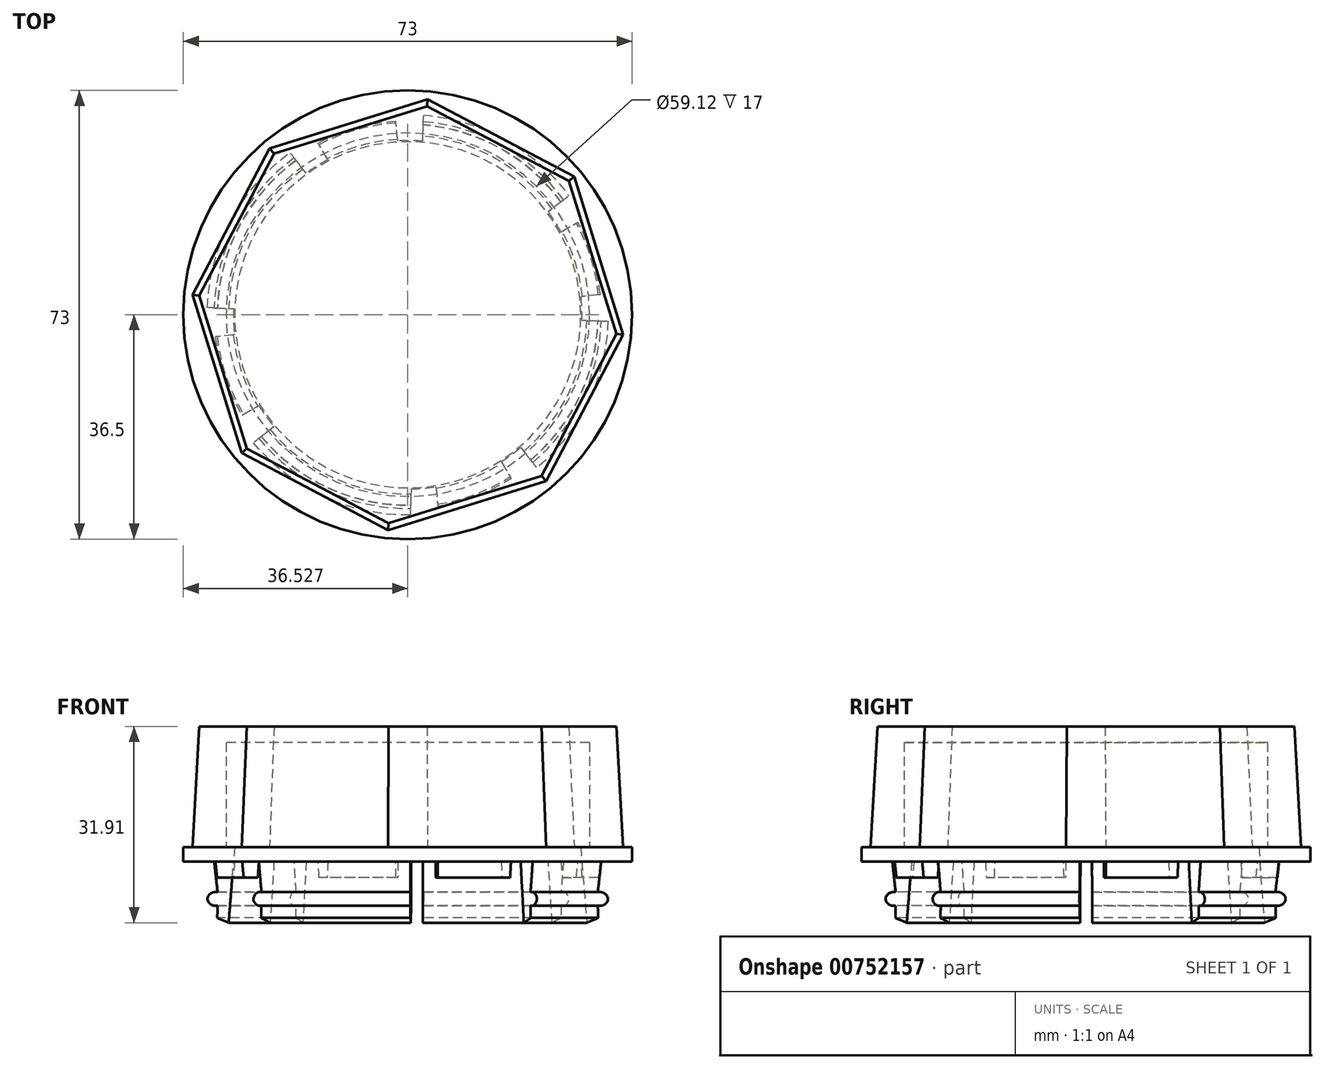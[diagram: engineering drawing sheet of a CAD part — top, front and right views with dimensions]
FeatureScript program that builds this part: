
annotation { "Feature Type Name" : "Feature", "Feature Type Description" : "" }
export const myFeature = defineFeature(function(context is Context, id is Id, definition is map)
    precondition{}
    {
        {
            var Q0;
            Q0=qCreatedBy(makeId("Top.planeOp"),FACE);
            var sketch = newSketch(context, id + "F0", { "sketchPlane" : qUnion([Q0])});
            skCircle(sketch, "E0.cCircle", {"center": v(41.88, 0) * mm, "radius": 35.18 * mm, "construction": true});
            skLineSegment(sketch, "E0.0", {"start": v(14.82, -22.49) * mm, "end": v(6.85, 3.23) * mm});
            skLineSegment(sketch, "E0.1", {"start": v(6.85, 3.23) * mm, "end": v(19.39, 27.05) * mm});
            skLineSegment(sketch, "E0.2", {"start": v(19.39, 27.05) * mm, "end": v(45.1, 35.03) * mm});
            skLineSegment(sketch, "E0.3", {"start": v(45.1, 35.03) * mm, "end": v(68.93, 22.49) * mm});
            skLineSegment(sketch, "E0.4", {"start": v(68.93, 22.49) * mm, "end": v(76.9, -3.23) * mm});
            skLineSegment(sketch, "E0.5", {"start": v(76.9, -3.23) * mm, "end": v(64.36, -27.05) * mm});
            skLineSegment(sketch, "E0.6", {"start": v(64.36, -27.05) * mm, "end": v(38.65, -35.03) * mm});
            skLineSegment(sketch, "E0.7", {"start": v(38.65, -35.03) * mm, "end": v(14.82, -22.49) * mm});
            skSolve(sketch);
        }
        {
            var Q0;
            Q0=qSketchRegion(id+"F0",true);
            extrude(context, id + "F1", {"entities" : qUnion([Q0]), "depth" : 19.6 * mm, "offsetDistance" : 25 * mm, "hasDraft" : true, "draftAngle" : 3 * degree, "draftPullDirection" : true});
        }
        {
            var Q0;
            Q0=qCreatedBy(makeId("Front.planeOp"),FACE);
            var sketch = newSketch(context, id + "F2", { "sketchPlane" : qUnion([Q0])});
            skLineSegment(sketch, "E1", {"start": v(71.3, 19.61) * mm, "end": v(71.3, 20.31) * mm});
            skLineSegment(sketch, "E2", {"start": v(71.3, 20.31) * mm, "end": v(70.7, 20.31) * mm});
            skLineSegment(sketch, "E3", {"start": v(70.7, 20.31) * mm, "end": v(70.7, 19.61) * mm});
            skLineSegment(sketch, "E4", {"start": v(61.4, 22) * mm, "end": v(61.4, 21.36) * mm});
            skLineSegment(sketch, "E5", {"start": v(61.4, 21.36) * mm, "end": v(41.94, 21.36) * mm});
            skArc(sketch, "E6", {"start": v(70.7, 19.61) * mm, "mid": v(66.19, 21.38) * mm, "end": v(61.4, 22) * mm});
            skLineSegment(sketch, "E7", {"start": v(41.94, 21.36) * mm, "end": v(41.94, 19.6) * mm});
            skSolve(sketch);
        }
        {
            var Q0;
            Q0=qSketchRegion(id+"F2",true);
            var Q1;
            Q1=sQuery(id+"F2.wireOp",EDGE,"E5");
            var Q2;
            Q2=sQuery(id+"F2.wireOp",EDGE,"E4");
            var Q3;
            Q3=sQuery(id+"F2.wireOp",EDGE,"E6");
            var Q4;
            Q4=sQuery(id+"F2.wireOp",EDGE,"E1");
            var Q5;
            Q5=sQuery(id+"F2.wireOp",EDGE,"E3");
            var Q6;
            Q6=sQuery(id+"F2.wireOp",EDGE,"E2");
            var Q7;
            Q7=sQuery(id+"F2.wireOp",EDGE,"E7");
            revolve(context, id + "F3", {"bodyType" : ToolBodyType.SURFACE, "surfaceOperationType" : NewSurfaceOperationType.NEW, "entities" : qUnion([Q0]), "surfaceEntities" : qUnion([Q1, Q2, Q3, Q4, Q5, Q6]), "axis" : qUnion([Q7]), "revolveType" : RevolveType.FULL});
        }
        {
            var Q0;
            Q0=qCreatedBy(makeId("Front.planeOp"),FACE);
            var sketch = newSketch(context, id + "F4", { "sketchPlane" : qUnion([Q0])});
            skLineSegment(sketch, "E8", {"start": v(41.85, 2.47) * mm, "end": v(41.85, -0.28) * mm});
            skLineSegment(sketch, "E9", {"start": v(13.92, 0) * mm, "end": v(10.66, 0) * mm});
            skLineSegment(sketch, "E10", {"start": v(13.7, 0) * mm, "end": v(12.7, -12.3) * mm});
            skLineSegment(sketch, "E11", {"start": v(12.7, -12.3) * mm, "end": v(10.85, -11.54) * mm});
            skLineSegment(sketch, "E12", {"start": v(10.85, -11.54) * mm, "end": v(10.9, -9.54) * mm});
            skLineSegment(sketch, "E13", {"start": v(10.9, -7.32) * mm, "end": v(10.35, -2.35) * mm});
            skLineSegment(sketch, "E14", {"start": v(41.85, 0) * mm, "end": v(5.35, 0) * mm});
            skLineSegment(sketch, "E15", {"start": v(41.85, 2.47) * mm, "end": v(41.85, -22.81) * mm});
            skPoint(sketch, "E16", {"position": v(5.35, -2.35) * mm});
            skLineSegment(sketch, "E17", {"start": v(5.35, -2.35) * mm, "end": v(10.35, -2.35) * mm});
            skLineSegment(sketch, "E18", {"start": v(5.35, 0) * mm, "end": v(5.35, -2.35) * mm});
            skPoint(sketch, "E19", {"position": v(10.85, 0) * mm});
            skFitSpline(sketch, "E20", {"points": [v(10.9, -7.32) * mm, v(9.26, -8.52) * mm, v(10.9, -9.54) * mm], "startDerivative": vector(-5.91, 0.78) * mm, "endDerivative": vector(4.99, 1.1) * mm});
            skSolve(sketch);
        }
        {
            var Q0;
            Q0=qSketchRegion(id+"F4",true);
            var Q1;
            Q1=sQuery(id+"F4.wireOp",EDGE,"E14");
            var Q2;
            Q2=sQuery(id+"F4.wireOp",EDGE,"4cd7ZZWE-5ar5-vtm7-FDXw-HXyrbe5Stu3w");
            var Q3;
            Q3=sQuery(id+"F4.wireOp",EDGE,"E13");
            var Q4;
            Q4=sQuery(id+"F4.wireOp",EDGE,"4DvQKk0b-5Hhs-ZDoF-mvT5-3W0hP7iMOcEj");
            var Q5;
            Q5=sQuery(id+"F4.wireOp",EDGE,"seUdqvdR-pzSz-YYxp-RZCM-9PM7dyDkCj1m");
            var Q6;
            Q6=sQuery(id+"F4.wireOp",EDGE,"E11");
            var Q7;
            Q7=sQuery(id+"F4.wireOp",EDGE,"E12");
            var Q8;
            Q8=sQuery(id+"F4.wireOp",EDGE,"E10");
            var Q9;
            Q9=sQuery(id+"F4.wireOp",EDGE,"E15");
            revolve(context, id + "F5", {"surfaceOperationType" : NewSurfaceOperationType.NEW, "entities" : qUnion([Q0]), "surfaceEntities" : qUnion([Q1, Q2, Q3, Q4, Q5, Q6, Q7, Q8]), "axis" : qUnion([Q9]), "revolveType" : RevolveType.FULL});
        }
        {
            var Q0;
            Q0=qCreatedBy(makeId("Top.planeOp"),FACE);
            var sketch = newSketch(context, id + "F6", { "sketchPlane" : qUnion([Q0])});
            skCircle(sketch, "E21", {"center": v(41.88, 0) * mm, "radius": 29.56 * mm});
            skSolve(sketch);
        }
        {
            var Q0;
            Q0=qSketchRegion(id+"F6",true);
            extrude(context, id + "F7", {"entities" : qUnion([Q0]), "operationType" : NewBodyOperationType.REMOVE, "depth" : 17 * mm, "offsetDistance" : 25 * mm});
        }
        {
            var Q0;
            Q0=qCreatedBy(makeId("Top.planeOp"),FACE);
            var sketch = newSketch(context, id + "F8", { "sketchPlane" : qUnion([Q0])});
            skText(sketch, "E22", { "text": "SAAB", "fontName": "OpenSans-Bold.ttf"});
            const initialGuessF8  = {"E22": [0.03239, -0.00298, 1, 0, 0.00593]};
            skSetInitialGuess(sketch, initialGuessF8);
            skSolve(sketch);
        }
        {
            var Q0;
            Q0=qCreatedBy(makeId("Top.planeOp"),FACE);
            var sketch = newSketch(context, id + "F9", { "sketchPlane" : qUnion([Q0])});
            skLineSegment(sketch, "E23", {"start": v(69.85, -34.13) * mm, "end": v(16.32, 34.78) * mm});
            skLineSegment(sketch, "E24", {"start": v(16.32, 34.78) * mm, "end": v(43.91, 43.26) * mm});
            skLineSegment(sketch, "E25", {"start": v(43.91, 43.26) * mm, "end": v(42.61, -43.16) * mm});
            skLineSegment(sketch, "E26", {"start": v(9.14, -26.59) * mm, "end": v(79.03, 27.7) * mm});
            skLineSegment(sketch, "E27", {"start": v(79.03, 27.7) * mm, "end": v(86.57, -0.61) * mm});
            skLineSegment(sketch, "E28", {"start": v(86.57, -0.61) * mm, "end": v(43.22, 0) * mm});
            skLineSegment(sketch, "E29", {"start": v(42.61, -43.16) * mm, "end": v(69.85, -34.13) * mm});
            skLineSegment(sketch, "E30", {"start": v(0, 0.68) * mm, "end": v(43.22, 0) * mm});
            skLineSegment(sketch, "E31", {"start": v(9.14, -26.59) * mm, "end": v(0, 0.68) * mm});
            skPoint(sketch, "E32", {"position": v(19.48, -18.55) * mm});
            skPoint(sketch, "E33", {"position": v(12.6, 0.48) * mm});
            skPoint(sketch, "E34", {"position": v(24.83, 23.83) * mm});
            skPoint(sketch, "E35", {"position": v(42.83, -28.88) * mm});
            skPoint(sketch, "E36", {"position": v(60.43, -22) * mm});
            skPoint(sketch, "E37", {"position": v(71.17, -0.4) * mm});
            skPoint(sketch, "E38", {"position": v(65.22, 16.98) * mm});
            skPoint(sketch, "E39", {"position": v(43.69, 28.4) * mm});
            skLineSegment(sketch, "E40", {"start": v(12.6, 0.48) * mm, "end": v(19.48, -18.55) * mm});
            skLineSegment(sketch, "E41", {"start": v(24.83, 23.83) * mm, "end": v(43.69, 28.4) * mm});
            skLineSegment(sketch, "E42", {"start": v(65.22, 16.98) * mm, "end": v(71.17, -0.4) * mm});
            skLineSegment(sketch, "E43", {"start": v(60.43, -22) * mm, "end": v(42.83, -28.88) * mm});
            skSolve(sketch);
        }
        {
            var Q0;
            Q0=qSketchRegion(id+"F9",true);
            extrude(context, id + "F10", {"entities" : qUnion([Q0]), "oppositeDirection" : true, "depth" : 25 * mm, "offsetDistance" : 25 * mm, "hasSecondDirection" : true, "secondDirectionOppositeDirection" : true, "secondDirectionDepth" : 5 * mm});
        }
        {
            var Q0;
            Q0=makeQuery(id+"F10.opExtrude","SWEPT_BODY",BODY,{"disambiguationData":[OSD([sQuery(id+"F9.wireOp",EDGE,"E23"),sQuery(id+"F9.wireOp",EDGE,"E25"),sQuery(id+"F9.wireOp",EDGE,"E26"),sQuery(id+"F9.wireOp",EDGE,"E28"),sQuery(id+"F9.wireOp",EDGE,"E29"),sQuery(id+"F9.wireOp",EDGE,"E30"),sQuery(id+"F9.wireOp",EDGE,"E31")])]});
            var Q1;
            Q1=makeQuery(id+"F10.opExtrude","SWEPT_BODY",BODY,{"disambiguationData":[OSD([sQuery(id+"F9.wireOp",EDGE,"E26"),sQuery(id+"F9.wireOp",EDGE,"E27"),sQuery(id+"F9.wireOp",EDGE,"E28")])]});
            var Q2;
            Q2=makeQuery(id+"F10.opExtrude","SWEPT_BODY",BODY,{"disambiguationData":[OSD([sQuery(id+"F9.wireOp",EDGE,"E23"),sQuery(id+"F9.wireOp",EDGE,"E24"),sQuery(id+"F9.wireOp",EDGE,"E25")])]});
            var Q3;
            Q3=makeQuery(id+"FadKjfFnsJpzDV8_9.opBoolean","SPLIT",BODY,{"disambiguationData":[OD(5.0)],"derivedFrom":makeQuery(id+"F5.opRevolve","SWEPT_BODY",BODY,{"disambiguationData":[OSD([sQuery(id+"F4.wireOp",EDGE,"E10"),sQuery(id+"F4.wireOp",EDGE,"E11"),sQuery(id+"F4.wireOp",EDGE,"E12"),sQuery(id+"F4.wireOp",EDGE,"seUdqvdR-pzSz-YYxp-RZCM-9PM7dyDkCj1m"),sQuery(id+"F4.wireOp",EDGE,"4DvQKk0b-5Hhs-ZDoF-mvT5-3W0hP7iMOcEj"),sQuery(id+"F4.wireOp",EDGE,"E13"),sQuery(id+"F4.wireOp",EDGE,"E14"),sQuery(id+"F4.wireOp",EDGE,"E17"),sQuery(id+"F4.wireOp",EDGE,"E18")])]})});
            var Q4;
            Q4=makeQuery(id+"FadKjfFnsJpzDV8_9.opBoolean","SPLIT",BODY,{"disambiguationData":[OD(3.0)],"derivedFrom":makeQuery(id+"F5.opRevolve","SWEPT_BODY",BODY,{"disambiguationData":[OSD([sQuery(id+"F4.wireOp",EDGE,"E10"),sQuery(id+"F4.wireOp",EDGE,"E11"),sQuery(id+"F4.wireOp",EDGE,"E12"),sQuery(id+"F4.wireOp",EDGE,"seUdqvdR-pzSz-YYxp-RZCM-9PM7dyDkCj1m"),sQuery(id+"F4.wireOp",EDGE,"4DvQKk0b-5Hhs-ZDoF-mvT5-3W0hP7iMOcEj"),sQuery(id+"F4.wireOp",EDGE,"E13"),sQuery(id+"F4.wireOp",EDGE,"E14"),sQuery(id+"F4.wireOp",EDGE,"E17"),sQuery(id+"F4.wireOp",EDGE,"E18")])]})});
            var Q5;
            Q5=makeQuery(id+"FadKjfFnsJpzDV8_9.opBoolean","SPLIT",BODY,{"disambiguationData":[OD(7.0)],"derivedFrom":makeQuery(id+"F5.opRevolve","SWEPT_BODY",BODY,{"disambiguationData":[OSD([sQuery(id+"F4.wireOp",EDGE,"E10"),sQuery(id+"F4.wireOp",EDGE,"E11"),sQuery(id+"F4.wireOp",EDGE,"E12"),sQuery(id+"F4.wireOp",EDGE,"seUdqvdR-pzSz-YYxp-RZCM-9PM7dyDkCj1m"),sQuery(id+"F4.wireOp",EDGE,"4DvQKk0b-5Hhs-ZDoF-mvT5-3W0hP7iMOcEj"),sQuery(id+"F4.wireOp",EDGE,"E13"),sQuery(id+"F4.wireOp",EDGE,"E14"),sQuery(id+"F4.wireOp",EDGE,"E17"),sQuery(id+"F4.wireOp",EDGE,"E18")])]})});
            var Q6;
            Q6=makeQuery(id+"FadKjfFnsJpzDV8_9.opBoolean","SPLIT",BODY,{"disambiguationData":[OD(2.0)],"derivedFrom":makeQuery(id+"F5.opRevolve","SWEPT_BODY",BODY,{"disambiguationData":[OSD([sQuery(id+"F4.wireOp",EDGE,"E10"),sQuery(id+"F4.wireOp",EDGE,"E11"),sQuery(id+"F4.wireOp",EDGE,"E12"),sQuery(id+"F4.wireOp",EDGE,"seUdqvdR-pzSz-YYxp-RZCM-9PM7dyDkCj1m"),sQuery(id+"F4.wireOp",EDGE,"4DvQKk0b-5Hhs-ZDoF-mvT5-3W0hP7iMOcEj"),sQuery(id+"F4.wireOp",EDGE,"E13"),sQuery(id+"F4.wireOp",EDGE,"E14"),sQuery(id+"F4.wireOp",EDGE,"E17"),sQuery(id+"F4.wireOp",EDGE,"E18")])]})});
            var Q7;
            Q7=makeQuery(id+"FadKjfFnsJpzDV8_9.opBoolean","SPLIT",BODY,{"disambiguationData":[OD(0.0)],"derivedFrom":makeQuery(id+"F5.opRevolve","SWEPT_BODY",BODY,{"disambiguationData":[OSD([sQuery(id+"F4.wireOp",EDGE,"E10"),sQuery(id+"F4.wireOp",EDGE,"E11"),sQuery(id+"F4.wireOp",EDGE,"E12"),sQuery(id+"F4.wireOp",EDGE,"seUdqvdR-pzSz-YYxp-RZCM-9PM7dyDkCj1m"),sQuery(id+"F4.wireOp",EDGE,"4DvQKk0b-5Hhs-ZDoF-mvT5-3W0hP7iMOcEj"),sQuery(id+"F4.wireOp",EDGE,"E13"),sQuery(id+"F4.wireOp",EDGE,"E14"),sQuery(id+"F4.wireOp",EDGE,"E17"),sQuery(id+"F4.wireOp",EDGE,"E18")])]})});
            var Q8;
            Q8=makeQuery(id+"FadKjfFnsJpzDV8_9.opBoolean","SPLIT",BODY,{"disambiguationData":[OD(6.0)],"derivedFrom":makeQuery(id+"F5.opRevolve","SWEPT_BODY",BODY,{"disambiguationData":[OSD([sQuery(id+"F4.wireOp",EDGE,"E10"),sQuery(id+"F4.wireOp",EDGE,"E11"),sQuery(id+"F4.wireOp",EDGE,"E12"),sQuery(id+"F4.wireOp",EDGE,"seUdqvdR-pzSz-YYxp-RZCM-9PM7dyDkCj1m"),sQuery(id+"F4.wireOp",EDGE,"4DvQKk0b-5Hhs-ZDoF-mvT5-3W0hP7iMOcEj"),sQuery(id+"F4.wireOp",EDGE,"E13"),sQuery(id+"F4.wireOp",EDGE,"E14"),sQuery(id+"F4.wireOp",EDGE,"E17"),sQuery(id+"F4.wireOp",EDGE,"E18")])]})});
            var Q9;
            Q9=makeQuery(id+"FadKjfFnsJpzDV8_9.opBoolean","SPLIT",BODY,{"disambiguationData":[OD(4.0)],"derivedFrom":makeQuery(id+"F5.opRevolve","SWEPT_BODY",BODY,{"disambiguationData":[OSD([sQuery(id+"F4.wireOp",EDGE,"E10"),sQuery(id+"F4.wireOp",EDGE,"E11"),sQuery(id+"F4.wireOp",EDGE,"E12"),sQuery(id+"F4.wireOp",EDGE,"seUdqvdR-pzSz-YYxp-RZCM-9PM7dyDkCj1m"),sQuery(id+"F4.wireOp",EDGE,"4DvQKk0b-5Hhs-ZDoF-mvT5-3W0hP7iMOcEj"),sQuery(id+"F4.wireOp",EDGE,"E13"),sQuery(id+"F4.wireOp",EDGE,"E14"),sQuery(id+"F4.wireOp",EDGE,"E17"),sQuery(id+"F4.wireOp",EDGE,"E18")])]})});
            var Q10;
            Q10=makeQuery(id+"FadKjfFnsJpzDV8_9.opBoolean","SPLIT",BODY,{"disambiguationData":[OD(1.0)],"derivedFrom":makeQuery(id+"F5.opRevolve","SWEPT_BODY",BODY,{"disambiguationData":[OSD([sQuery(id+"F4.wireOp",EDGE,"E10"),sQuery(id+"F4.wireOp",EDGE,"E11"),sQuery(id+"F4.wireOp",EDGE,"E12"),sQuery(id+"F4.wireOp",EDGE,"seUdqvdR-pzSz-YYxp-RZCM-9PM7dyDkCj1m"),sQuery(id+"F4.wireOp",EDGE,"4DvQKk0b-5Hhs-ZDoF-mvT5-3W0hP7iMOcEj"),sQuery(id+"F4.wireOp",EDGE,"E13"),sQuery(id+"F4.wireOp",EDGE,"E14"),sQuery(id+"F4.wireOp",EDGE,"E17"),sQuery(id+"F4.wireOp",EDGE,"E18")])]})});
            booleanBodies(context, id + "F11", {"operationType" : BooleanOperationType.SUBTRACTION, "tools" : qUnion([Q0, Q1, Q2]), "targets" : qUnion([Q3, Q4, Q5, Q6, Q7, Q8, Q9, Q10])});
        }
        {
            var Q0;
            Q0=qCreatedBy(makeId("Top.planeOp"),FACE);
            var sketch = newSketch(context, id + "F12", { "sketchPlane" : qUnion([Q0])});
            skPoint(sketch, "E44.endSnap0", {"position": v(222.12, 4.24) * mm});
            skPoint(sketch, "E45", {"position": v(43.35, 0) * mm});
            skLineSegment(sketch, "E46", {"start": v(76.6, 26.03) * mm, "end": v(5.98, -29.26) * mm});
            skLineSegment(sketch, "E47", {"start": v(43.35, 0) * mm, "end": v(74.1, -39.28) * mm});
            skLineSegment(sketch, "E48", {"start": v(43.35, 0) * mm, "end": v(14.72, 36.58) * mm});
            skLineSegment(sketch, "E49", {"start": v(1.61, -23.99) * mm, "end": v(43.35, 0) * mm});
            skLineSegment(sketch, "E50", {"start": v(43.35, 0) * mm, "end": v(69.77, -45.97) * mm});
            skLineSegment(sketch, "E51", {"start": v(43.35, 0) * mm, "end": v(81.27, 21.79) * mm});
            skLineSegment(sketch, "E52", {"start": v(43.35, 0) * mm, "end": v(20.03, 40.59) * mm});
            skLineSegment(sketch, "E53", {"start": v(14.72, 36.58) * mm, "end": v(20.03, 40.59) * mm});
            skLineSegment(sketch, "E54", {"start": v(76.6, 26.03) * mm, "end": v(81.27, 21.79) * mm});
            skLineSegment(sketch, "E55", {"start": v(74.1, -39.28) * mm, "end": v(69.77, -45.97) * mm});
            skLineSegment(sketch, "E56", {"start": v(5.98, -29.26) * mm, "end": v(1.61, -23.99) * mm});
            skLineSegment(sketch, "E57", {"start": v(85.32, 4.6) * mm, "end": v(-3.82, -5.18) * mm});
            skLineSegment(sketch, "E58", {"start": v(43.35, 0) * mm, "end": v(48.8, -49.6) * mm});
            skLineSegment(sketch, "E59", {"start": v(43.35, 0) * mm, "end": v(38.29, 46.18) * mm});
            skLineSegment(sketch, "E60", {"start": v(-4.76, 1.6) * mm, "end": v(43.35, 0) * mm});
            skLineSegment(sketch, "E61", {"start": v(43.35, 0) * mm, "end": v(41.59, -52.99) * mm});
            skLineSegment(sketch, "E62", {"start": v(43.35, 0) * mm, "end": v(87.06, -1.46) * mm});
            skLineSegment(sketch, "E63", {"start": v(43.35, 0) * mm, "end": v(44.92, 46.79) * mm});
            skLineSegment(sketch, "E64", {"start": v(38.29, 46.18) * mm, "end": v(44.92, 46.79) * mm});
            skLineSegment(sketch, "E65", {"start": v(85.32, 4.6) * mm, "end": v(87.06, -1.46) * mm});
            skLineSegment(sketch, "E66", {"start": v(48.8, -49.6) * mm, "end": v(41.59, -52.99) * mm});
            skLineSegment(sketch, "E67", {"start": v(-3.82, -5.18) * mm, "end": v(-4.76, 1.6) * mm});
            skSolve(sketch);
        }
        {
            var Q0;
            Q0=qSketchRegion(id+"F12",true);
            extrude(context, id + "F13", {"entities" : qUnion([Q0]), "oppositeDirection" : true, "depth" : 10 * mm, "offsetDistance" : 25 * mm});
        }
        {
            var Q0;
            Q0=makeQuery(id+"F13.opExtrude","SWEPT_BODY",BODY,{"disambiguationData":[OSD([sQuery(id+"F12.wireOp",EDGE,"E48"),sQuery(id+"F12.wireOp",EDGE,"E52"),sQuery(id+"F12.wireOp",EDGE,"E53")])]});
            var Q1;
            Q1=makeQuery(id+"F13.opExtrude","SWEPT_BODY",BODY,{"disambiguationData":[OSD([sQuery(id+"F12.wireOp",EDGE,"E57"),sQuery(id+"F12.wireOp",EDGE,"E60"),sQuery(id+"F12.wireOp",EDGE,"E67")])]});
            var Q2;
            Q2=makeQuery(id+"F13.opExtrude","SWEPT_BODY",BODY,{"disambiguationData":[OSD([sQuery(id+"F12.wireOp",EDGE,"E46"),sQuery(id+"F12.wireOp",EDGE,"E49"),sQuery(id+"F12.wireOp",EDGE,"E56")])]});
            var Q3;
            Q3=makeQuery(id+"F13.opExtrude","SWEPT_BODY",BODY,{"disambiguationData":[OSD([sQuery(id+"F12.wireOp",EDGE,"E58"),sQuery(id+"F12.wireOp",EDGE,"E61"),sQuery(id+"F12.wireOp",EDGE,"E66")])]});
            var Q4;
            Q4=makeQuery(id+"F13.opExtrude","SWEPT_BODY",BODY,{"disambiguationData":[OSD([sQuery(id+"F12.wireOp",EDGE,"E47"),sQuery(id+"F12.wireOp",EDGE,"E50"),sQuery(id+"F12.wireOp",EDGE,"E55")])]});
            var Q5;
            Q5=makeQuery(id+"F13.opExtrude","SWEPT_BODY",BODY,{"disambiguationData":[OSD([sQuery(id+"F12.wireOp",EDGE,"E57"),sQuery(id+"F12.wireOp",EDGE,"E62"),sQuery(id+"F12.wireOp",EDGE,"E65")])]});
            var Q6;
            Q6=makeQuery(id+"F13.opExtrude","SWEPT_BODY",BODY,{"disambiguationData":[OSD([sQuery(id+"F12.wireOp",EDGE,"E46"),sQuery(id+"F12.wireOp",EDGE,"E51"),sQuery(id+"F12.wireOp",EDGE,"E54")])]});
            var Q7;
            Q7=makeQuery(id+"F13.opExtrude","SWEPT_BODY",BODY,{"disambiguationData":[OSD([sQuery(id+"F12.wireOp",EDGE,"E59"),sQuery(id+"F12.wireOp",EDGE,"E63"),sQuery(id+"F12.wireOp",EDGE,"E64")])]});
            transform(context, id + "F14", {"entities" : qUnion([Q0, Q1, Q2, Q3, Q4, Q5, Q6, Q7]), "transformType" : TransformType.TRANSLATION_3D, "dx" : 0 * mm, "dy" : 0 * mm, "dz" : -2.35 * mm, "makeCopy" : false});
        }
        {
            var Q0;
            Q0=makeQuery(id+"F13.opExtrude","SWEPT_BODY",BODY,{"disambiguationData":[OSD([sQuery(id+"F12.wireOp",EDGE,"E48"),sQuery(id+"F12.wireOp",EDGE,"E52"),sQuery(id+"F12.wireOp",EDGE,"E53")])]});
            var Q1;
            Q1=makeQuery(id+"F13.opExtrude","SWEPT_BODY",BODY,{"disambiguationData":[OSD([sQuery(id+"F12.wireOp",EDGE,"E57"),sQuery(id+"F12.wireOp",EDGE,"E60"),sQuery(id+"F12.wireOp",EDGE,"E67")])]});
            var Q2;
            Q2=makeQuery(id+"F13.opExtrude","SWEPT_BODY",BODY,{"disambiguationData":[OSD([sQuery(id+"F12.wireOp",EDGE,"E46"),sQuery(id+"F12.wireOp",EDGE,"E49"),sQuery(id+"F12.wireOp",EDGE,"E56")])]});
            var Q3;
            Q3=makeQuery(id+"F13.opExtrude","SWEPT_BODY",BODY,{"disambiguationData":[OSD([sQuery(id+"F12.wireOp",EDGE,"E58"),sQuery(id+"F12.wireOp",EDGE,"E61"),sQuery(id+"F12.wireOp",EDGE,"E66")])]});
            var Q4;
            Q4=makeQuery(id+"F13.opExtrude","SWEPT_BODY",BODY,{"disambiguationData":[OSD([sQuery(id+"F12.wireOp",EDGE,"E47"),sQuery(id+"F12.wireOp",EDGE,"E50"),sQuery(id+"F12.wireOp",EDGE,"E55")])]});
            var Q5;
            Q5=makeQuery(id+"F13.opExtrude","SWEPT_BODY",BODY,{"disambiguationData":[OSD([sQuery(id+"F12.wireOp",EDGE,"E57"),sQuery(id+"F12.wireOp",EDGE,"E62"),sQuery(id+"F12.wireOp",EDGE,"E65")])]});
            var Q6;
            Q6=makeQuery(id+"F13.opExtrude","SWEPT_BODY",BODY,{"disambiguationData":[OSD([sQuery(id+"F12.wireOp",EDGE,"E46"),sQuery(id+"F12.wireOp",EDGE,"E51"),sQuery(id+"F12.wireOp",EDGE,"E54")])]});
            var Q7;
            Q7=makeQuery(id+"F13.opExtrude","SWEPT_BODY",BODY,{"disambiguationData":[OSD([sQuery(id+"F12.wireOp",EDGE,"E59"),sQuery(id+"F12.wireOp",EDGE,"E63"),sQuery(id+"F12.wireOp",EDGE,"E64")])]});
            var Q8;
            Q8=makeQuery(id+"F5.opRevolve","SWEPT_BODY",BODY,{"disambiguationData":[OSD([sQuery(id+"F4.wireOp",EDGE,"E10"),sQuery(id+"F4.wireOp",EDGE,"E11"),sQuery(id+"F4.wireOp",EDGE,"E12"),sQuery(id+"F4.wireOp",EDGE,"seUdqvdR-pzSz-YYxp-RZCM-9PM7dyDkCj1m"),sQuery(id+"F4.wireOp",EDGE,"4DvQKk0b-5Hhs-ZDoF-mvT5-3W0hP7iMOcEj"),sQuery(id+"F4.wireOp",EDGE,"E13"),sQuery(id+"F4.wireOp",EDGE,"E14"),sQuery(id+"F4.wireOp",EDGE,"E17"),sQuery(id+"F4.wireOp",EDGE,"E18")])]});
            booleanBodies(context, id + "F15", {"operationType" : BooleanOperationType.SUBTRACTION, "tools" : qUnion([Q0, Q1, Q2, Q3, Q4, Q5, Q6, Q7]), "targets" : qUnion([Q8])});
        }
    });
